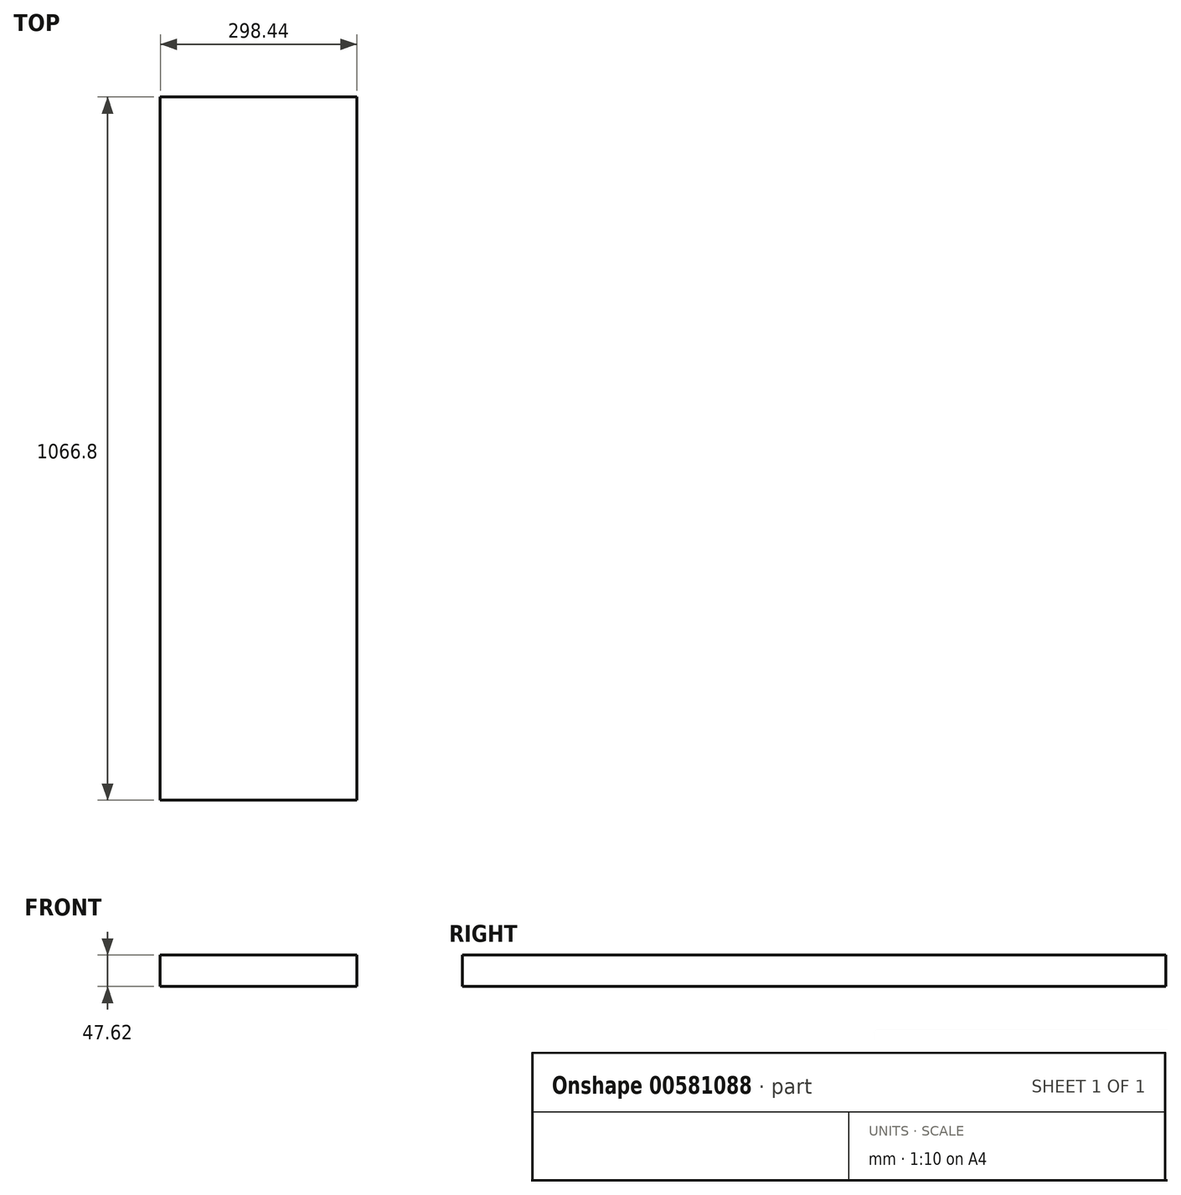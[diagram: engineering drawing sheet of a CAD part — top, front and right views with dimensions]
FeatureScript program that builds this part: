
annotation { "Feature Type Name" : "Feature", "Feature Type Description" : "" }
export const myFeature = defineFeature(function(context is Context, id is Id, definition is map)
    precondition{}
    {
        {
            var Q0;
            Q0=qCreatedBy(makeId("Front.planeOp"),FACE);
            var sketch = newSketch(context, id + "F0", { "sketchPlane" : qUnion([Q0])});
            skLineSegment(sketch, "E0.bottom", {"start": v(149.23, 23.81) * mm, "end": v(-149.22, 23.81) * mm});
            skLineSegment(sketch, "E0.top", {"start": v(149.23, -23.81) * mm, "end": v(-149.22, -23.81) * mm});
            skLineSegment(sketch, "E0.left", {"start": v(149.23, 23.81) * mm, "end": v(149.23, -23.81) * mm});
            skLineSegment(sketch, "E0.right", {"start": v(-149.22, 23.81) * mm, "end": v(-149.22, -23.81) * mm});
            skPoint(sketch, "E0.middle", {"position": v(0, 0) * mm});
            skSolve(sketch);
        }
        {
            var Q0;
            Q0=makeQuery(id+"F0.imprint","IMPRINT",FACE,{"disambiguationData":[TD([[makeQuery(id+"F0.imprint","IMPRINT",EDGE,{"derivedFrom":sQuery(id+"F0.wireOp",EDGE,"E0.bottom")}),1.0]])]});
            extrude(context, id + "F1", {"entities" : qUnion([Q0]), "depth" : 1066.8 * mm, "offsetDistance" : 25.4 * mm});
        }
    });
